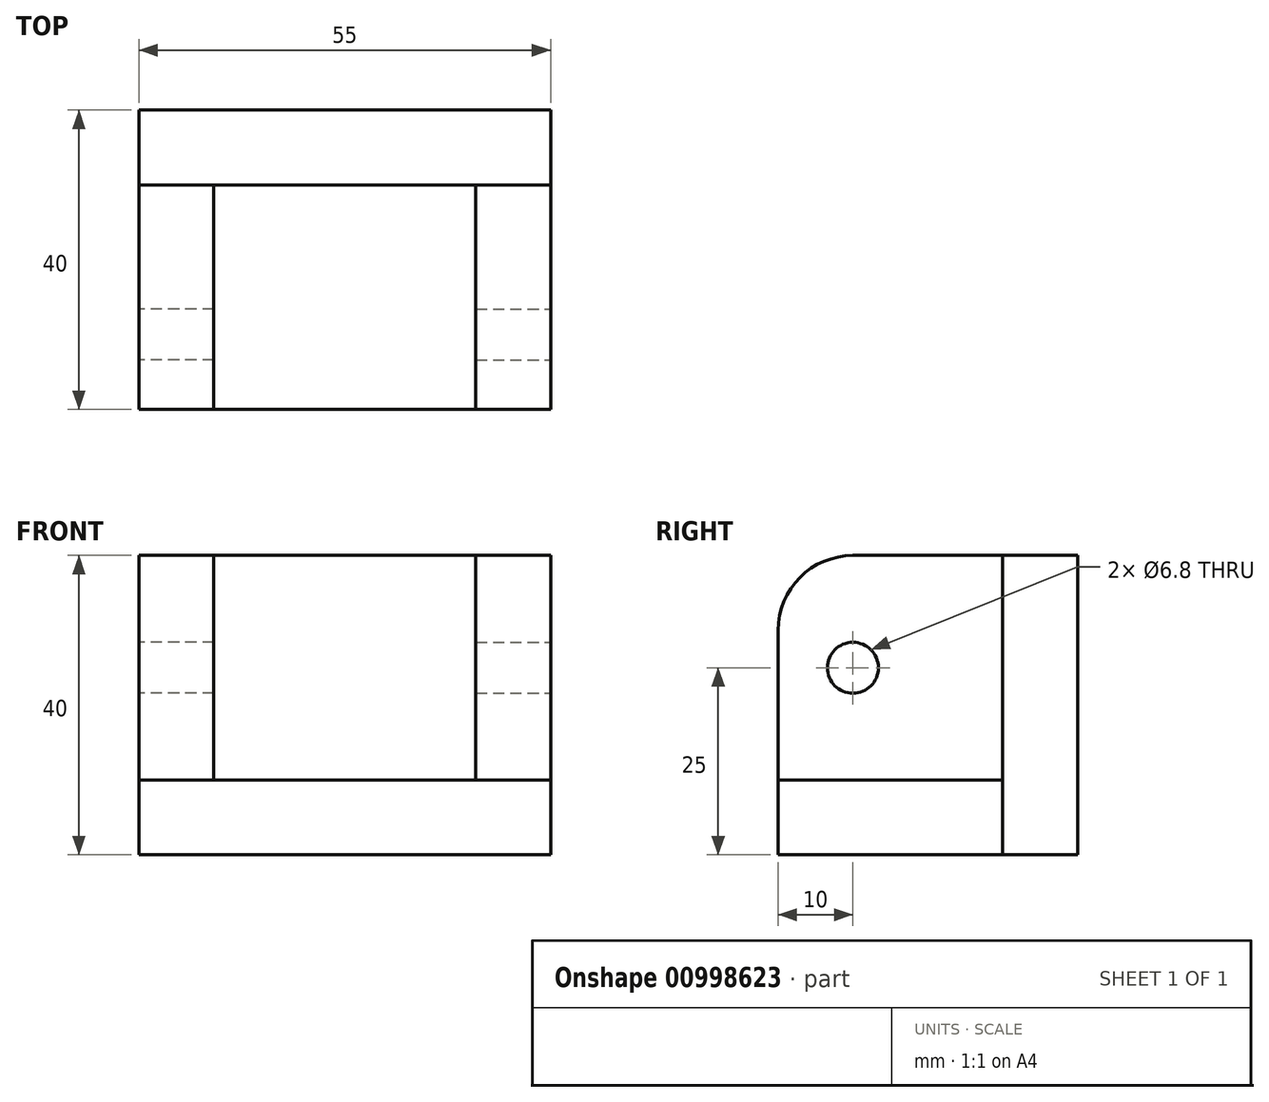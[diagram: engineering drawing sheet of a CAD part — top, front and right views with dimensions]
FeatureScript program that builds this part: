
annotation { "Feature Type Name" : "Feature", "Feature Type Description" : "" }
export const myFeature = defineFeature(function(context is Context, id is Id, definition is map)
    precondition{}
    {
        {
            var Q0;
            Q0=qCreatedBy(makeId("Top.planeOp"),FACE);
            var sketch = newSketch(context, id + "F0", { "sketchPlane" : qUnion([Q0])});
            skLineSegment(sketch, "E0.bottom", {"start": v(-27.5, 15) * mm, "end": v(27.5, 15) * mm});
            skLineSegment(sketch, "E0.top", {"start": v(-27.5, -15) * mm, "end": v(27.5, -15) * mm});
            skLineSegment(sketch, "E0.left", {"start": v(-27.5, 15) * mm, "end": v(-27.5, -15) * mm});
            skLineSegment(sketch, "E0.right", {"start": v(27.5, 15) * mm, "end": v(27.5, -15) * mm});
            skPoint(sketch, "E0.middle", {"position": v(0, 0) * mm});
            skSolve(sketch);
        }
        {
            var Q0;
            Q0=makeQuery(id+"F0.imprint","IMPRINT",FACE,{"disambiguationData":[TD([[makeQuery(id+"F0.imprint","IMPRINT",EDGE,{"derivedFrom":sQuery(id+"F0.wireOp",EDGE,"E0.bottom")}),-1.0]])]});
            extrude(context, id + "F1", {"entities" : qUnion([Q0]), "depth" : 10 * mm, "offsetDistance" : 25 * mm});
        }
        {
            var Q0;
            Q0=makeQuery(id+"F1.opExtrude","SWEPT_FACE",FACE,{"disambiguationData":[OSD([sQuery(id+"F0.wireOp",EDGE,"E0.bottom")])]});
            var sketch = newSketch(context, id + "F2", { "sketchPlane" : qUnion([Q0])});
            skLineSegment(sketch, "E1", {"start": v(-27.5, 0) * mm, "end": v(-27.5, 40) * mm});
            skLineSegment(sketch, "E2", {"start": v(-27.5, 40) * mm, "end": v(27.5, 40) * mm});
            skLineSegment(sketch, "E3", {"start": v(27.5, 40) * mm, "end": v(27.5, 0) * mm});
            skLineSegment(sketch, "E4", {"start": v(27.5, 0) * mm, "end": v(-27.5, 0) * mm});
            skSolve(sketch);
        }
        {
            var Q0;
            {var subQ2=sQuery(id+"F2.wireOp",EDGE,"E2");Q0=makeQuery(id+"F2.imprint","IMPRINT",FACE,{"disambiguationData":[TD([[makeQuery(id+"F2.imprint","IMPRINT",EDGE,{"derivedFrom":subQ2}),-1.0]])]});}
            var Q1;
            {var subQ0=sQuery(id+"F2.wireOp",EDGE,"E4");Q1=makeQuery(id+"F2.imprint","IMPRINT",FACE,{"disambiguationData":[TD([[makeQuery(id+"F2.imprint","IMPRINT",EDGE,{"derivedFrom":subQ0}),-1.0]])]});}
            extrude(context, id + "F3", {"entities" : qUnion([Q0, Q1]), "depth" : 10 * mm, "offsetDistance" : 25 * mm});
        }
        {
            var Q0;
            Q0=makeQuery(id+"F1.opExtrude","SWEPT_FACE",FACE,{"disambiguationData":[OSD([sQuery(id+"F0.wireOp",EDGE,"E0.right")])]});
            var sketch = newSketch(context, id + "F4", { "sketchPlane" : qUnion([Q0])});
            skLineSegment(sketch, "E5", {"start": v(15, 10) * mm, "end": v(15, 40) * mm});
            skLineSegment(sketch, "E6", {"start": v(15, 40) * mm, "end": v(-15, 40) * mm});
            skLineSegment(sketch, "E7", {"start": v(-15, 40) * mm, "end": v(-15, 10) * mm});
            skLineSegment(sketch, "E8", {"start": v(-15, 10) * mm, "end": v(15, 10) * mm});
            skSolve(sketch);
        }
        {
            var Q0;
            Q0=makeQuery(id+"F4.imprint","IMPRINT",FACE,{"disambiguationData":[TD([[makeQuery(id+"F4.imprint","IMPRINT",EDGE,{"derivedFrom":sQuery(id+"F4.wireOp",EDGE,"E5")}),1.0]])]});
            extrude(context, id + "F5", {"entities" : qUnion([Q0]), "oppositeDirection" : true, "depth" : 10 * mm, "offsetDistance" : 25 * mm});
        }
        {
            var Q0;
            Q0=makeQuery(id+"F5.opExtrude","SWEPT_EDGE",EDGE,{"disambiguationData":[OSD([sQuery(id+"F4.wireOp",EDGE,"E6"),sQuery(id+"F4.wireOp",EDGE,"E7")])]});
            fillet(context, id + "F6", {"entities" : qUnion([Q0]), "radius" : 10 * mm, "tangentPropagation" : true, "allowEdgeOverflow" : false});
        }
        {
            var Q0;
            Q0=makeQuery(id+"F5.opExtrude","CAP_FACE",FACE,{"disambiguationData":[OSD([sQuery(id+"F4.wireOp",EDGE,"E5"),sQuery(id+"F4.wireOp",EDGE,"E6"),sQuery(id+"F4.wireOp",EDGE,"E7"),sQuery(id+"F4.wireOp",EDGE,"E8")])],"isStart":true});
            var sketch = newSketch(context, id + "F7", { "sketchPlane" : qUnion([Q0])});
            skPoint(sketch, "E9", {"position": v(-5, 25) * mm});
            skSolve(sketch);
        }
        {
            var Q0;
            Q0=sQuery(id+"F7.wireOp",VERTEX,"E9");
            var Q1;
            Q1=makeQuery(id+"F5.opExtrude","SWEPT_BODY",BODY,{"disambiguationData":[OSD([sQuery(id+"F4.wireOp",EDGE,"E5"),sQuery(id+"F4.wireOp",EDGE,"E6"),sQuery(id+"F4.wireOp",EDGE,"E7"),sQuery(id+"F4.wireOp",EDGE,"E8")])]});
            hole(context, id + "F8", {"style" : HoleStyle.SIMPLE, "endStyle" : HoleEndStyle.THROUGH, "standardTappedOrClearance" : lookupTablePath({ "standard" : "ISO", "engagement" : "75%", "pitch" : "1.25 mm", "size" : "M8", "type" : "Tapped" }), "standardBlindInLast" : lookupTablePath({ "standard" : "ISO", "fit" : "Normal", "engagement" : "75%", "pitch" : "1.25 mm", "size" : "M8", "type" : "Clearance & tapped" }), "holeDiameter" : 6.8 * mm, "majorDiameter" : 8 * mm, "showTappedDepth" : true, "isTappedThrough" : true, "tappedDepth" : 12 * mm, "tapClearance" : 3, "locations" : qUnion([Q0]), "scope" : qUnion([Q1])});
        }
        {
            var Q0;
            Q0=makeQuery(id+"F5.opExtrude","SWEPT_BODY",BODY,{"disambiguationData":[OSD([sQuery(id+"F4.wireOp",EDGE,"E5"),sQuery(id+"F4.wireOp",EDGE,"E6"),sQuery(id+"F4.wireOp",EDGE,"E7"),sQuery(id+"F4.wireOp",EDGE,"E8")])]});
            var Q1;
            Q1=qCreatedBy(makeId("Right.planeOp"),FACE);
            mirror(context, id + "F9", {"entities" : qUnion([Q0]), "mirrorPlane" : qUnion([Q1])});
        }
    });
